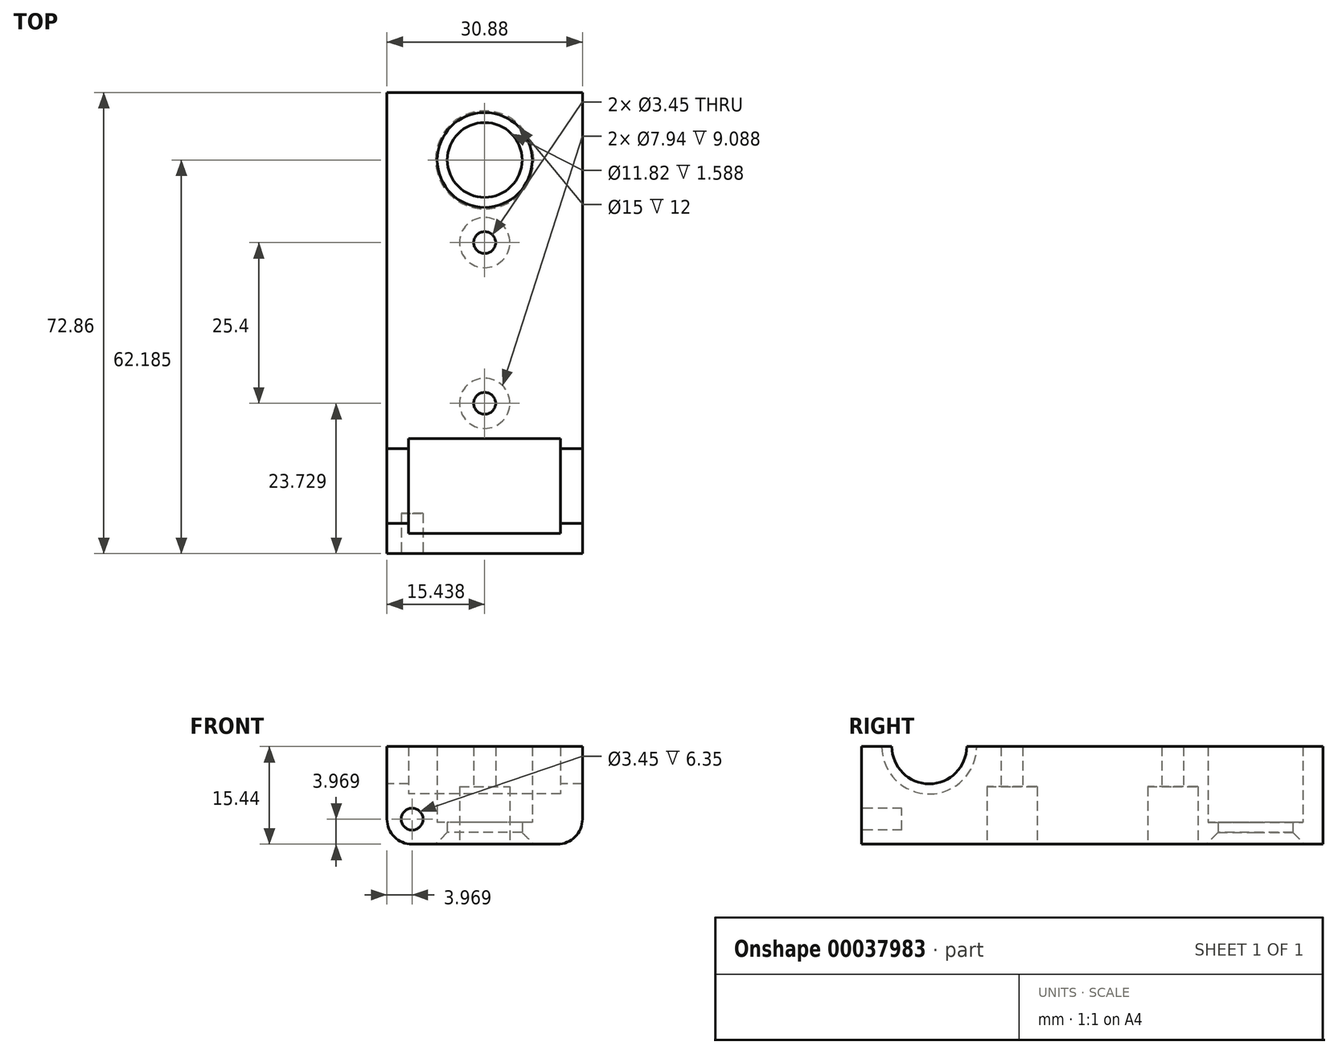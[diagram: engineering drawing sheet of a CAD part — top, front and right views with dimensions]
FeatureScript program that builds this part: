
annotation { "Feature Type Name" : "Feature", "Feature Type Description" : "" }
export const myFeature = defineFeature(function(context is Context, id is Id, definition is map)
    precondition{}
    {
        {
            var Q0;
            Q0=qCreatedBy(makeId("Top.planeOp"),FACE);
            var sketch = newSketch(context, id + "F0", { "sketchPlane" : qUnion([Q0])});
            skLineSegment(sketch, "E0.bottom", {"start": v(0, 0) * mm, "end": v(30.88, 0) * mm});
            skLineSegment(sketch, "E0.top", {"start": v(0, -72.86) * mm, "end": v(30.88, -72.86) * mm});
            skLineSegment(sketch, "E0.left", {"start": v(0, 0) * mm, "end": v(0, -72.86) * mm});
            skLineSegment(sketch, "E0.right", {"start": v(30.88, 0) * mm, "end": v(30.88, -72.86) * mm});
            skLineSegment(sketch, "E1", {"start": v(15.44, 0) * mm, "end": v(15.44, -10.67) * mm, "construction": true});
            skCircle(sketch, "E2", {"center": v(15.44, -10.67) * mm, "radius": 5.91 * mm});
            skLineSegment(sketch, "E3", {"start": v(15.44, -10.67) * mm, "end": v(15.44, -23.73) * mm, "construction": true});
            skLineSegment(sketch, "E4", {"start": v(15.44, -23.73) * mm, "end": v(15.44, -49.13) * mm, "construction": true});
            skCircle(sketch, "E5", {"center": v(15.44, -10.67) * mm, "radius": 7.5 * mm, "construction": true});
            skLineSegment(sketch, "E6", {"start": v(15.44, -49.13) * mm, "end": v(15.44, -72.86) * mm, "construction": true});
            skCircle(sketch, "E7", {"center": v(15.44, -23.73) * mm, "radius": 1.73 * mm});
            skCircle(sketch, "E8", {"center": v(15.44, -49.13) * mm, "radius": 1.73 * mm});
            skSolve(sketch);
        }
        {
            var Q0;
            Q0 = qSketchRegion(id + "F0", true);
            extrude(context, id + "F1", {"entities" : qUnion([Q0]), "depth" : 3.44 * mm});
        }
        {
            var Q0;
            Q0=makeQuery(id+"F1.opExtrude","CAP_FACE",FACE,{"disambiguationData":[OSD([sQuery(id+"F0.wireOp",EDGE,"E0.bottom"),sQuery(id+"F0.wireOp",EDGE,"E0.top"),sQuery(id+"F0.wireOp",EDGE,"E0.left"),sQuery(id+"F0.wireOp",EDGE,"E0.right"),sQuery(id+"F0.wireOp",EDGE,"E2"),sQuery(id+"F0.wireOp",EDGE,"E7"),sQuery(id+"F0.wireOp",EDGE,"E8")])],"isStart":false});
            var sketch = newSketch(context, id + "F2", { "sketchPlane" : qUnion([Q0])});
            skCircle(sketch, "E9", {"center": v(15.44, -10.67) * mm, "radius": 7.5 * mm});
            skSolve(sketch);
        }
        {
            var Q0;
            Q0=makeQuery(id+"F2.imprint","IMPRINT",FACE,{"disambiguationData":[TD([[makeQuery(id+"F2.imprint","IMPRINT",EDGE,{"derivedFrom":sQuery(id+"F2.wireOp",EDGE,"E9")}),-1.0]])]});
            extrude(context, id + "F3", {"entities" : qUnion([Q0]), "operationType" : NewBodyOperationType.ADD, "depth" : 12 * mm});
        }
        {
            var Q0;
            Q0=makeQuery(id+"F3.opExtrude","CAP_FACE",FACE,{"disambiguationData":[OSD([sQuery(id+"F0.wireOp",EDGE,"E0.bottom"),sQuery(id+"F0.wireOp",EDGE,"E0.top"),sQuery(id+"F0.wireOp",EDGE,"E0.left"),sQuery(id+"F0.wireOp",EDGE,"E0.right"),sQuery(id+"F0.wireOp",EDGE,"E7"),sQuery(id+"F0.wireOp",EDGE,"E8"),sQuery(id+"F2.wireOp",EDGE,"E9")])],"isStart":false});
            var sketch = newSketch(context, id + "F4", { "sketchPlane" : qUnion([Q0])});
            skLineSegment(sketch, "E10.bottom", {"start": v(3.44, -69.69) * mm, "end": v(27.44, -69.69) * mm});
            skLineSegment(sketch, "E10.top", {"start": v(3.44, -54.69) * mm, "end": v(27.44, -54.69) * mm});
            skLineSegment(sketch, "E10.left", {"start": v(3.44, -69.69) * mm, "end": v(3.44, -54.69) * mm});
            skLineSegment(sketch, "E10.right", {"start": v(27.44, -69.69) * mm, "end": v(27.44, -54.69) * mm});
            skLineSegment(sketch, "E11", {"start": v(15.44, -69.69) * mm, "end": v(15.44, -72.86) * mm, "construction": true});
            skSolve(sketch);
        }
        {
            var Q0;
            Q0 = qSketchRegion(id + "F4", true);
            extrude(context, id + "F5", {"entities" : qUnion([Q0]), "operationType" : NewBodyOperationType.REMOVE, "oppositeDirection" : true, "depth" : 7.5 * mm});
        }
        {
            var Q0;
            Q0=makeQuery(id+"F5.boolean.opBoolean","COPY",EDGE,{"derivedFrom":makeQuery(id+"F5.opExtrude","CAP_EDGE",EDGE,{"disambiguationData":[OSD([sQuery(id+"F4.wireOp",EDGE,"E10.top")])],"isStart":false})});
            var Q1;
            Q1=makeQuery(id+"F5.boolean.opBoolean","COPY",EDGE,{"derivedFrom":makeQuery(id+"F5.opExtrude","CAP_EDGE",EDGE,{"disambiguationData":[OSD([sQuery(id+"F4.wireOp",EDGE,"E10.bottom")])],"isStart":false})});
            fillet(context, id + "F6", {"entities" : qUnion([Q0, Q1]), "radius" : 7.5 * mm, "tangentPropagation" : true, "allowEdgeOverflow" : false});
        }
        {
            var Q0;
            {var subQ0=sQuery(id+"F0.wireOp",EDGE,"E0.left");Q0=makeQuery(id+"F3.boolean.opBoolean","MERGE",FACE,{"derivedFrom":[makeQuery(id+"F1.opExtrude","SWEPT_FACE",FACE,{"disambiguationData":[OSD([subQ0])]}),makeQuery(id+"F3.opExtrude","SWEPT_FACE",FACE,{"disambiguationData":[OSD([subQ0])]})]});}
            var sketch = newSketch(context, id + "F7", { "sketchPlane" : qUnion([Q0])});
            skArc(sketch, "E12", {"start": v(56.28, 15.44) * mm, "mid": v(62.19, 9.53) * mm, "end": v(68.1, 15.44) * mm});
            skLineSegment(sketch, "E13", {"start": v(56.28, 15.44) * mm, "end": v(68.1, 15.44) * mm});
            skSolve(sketch);
        }
        {
            var Q0;
            Q0 = qSketchRegion(id + "F7", true);
            var Q1;
            {var subQ0=sQuery(id+"F0.wireOp",EDGE,"E0.right");Q1=makeQuery(id+"F3.boolean.opBoolean","MERGE",FACE,{"derivedFrom":[makeQuery(id+"F1.opExtrude","SWEPT_FACE",FACE,{"disambiguationData":[OSD([subQ0])]}),makeQuery(id+"F3.opExtrude","SWEPT_FACE",FACE,{"disambiguationData":[OSD([subQ0])]})]});}
            extrude(context, id + "F8", {"entities" : qUnion([Q0]), "operationType" : NewBodyOperationType.REMOVE, "endBound" : BoundingType.UP_TO_SURFACE, "oppositeDirection" : true, "endBoundEntityFace" : qUnion([Q1]), "depth" : 25.4 * mm});
        }
        {
            var Q0;
            Q0=makeQuery(id+"F1.opExtrude","CAP_FACE",FACE,{"disambiguationData":[OSD([sQuery(id+"F0.wireOp",EDGE,"E0.bottom"),sQuery(id+"F0.wireOp",EDGE,"E0.top"),sQuery(id+"F0.wireOp",EDGE,"E0.left"),sQuery(id+"F0.wireOp",EDGE,"E0.right"),sQuery(id+"F0.wireOp",EDGE,"E2"),sQuery(id+"F0.wireOp",EDGE,"E7"),sQuery(id+"F0.wireOp",EDGE,"E8")])],"isStart":true});
            var sketch = newSketch(context, id + "F9", { "sketchPlane" : qUnion([Q0])});
            skCircle(sketch, "E14", {"center": v(15.44, 23.73) * mm, "radius": 3.97 * mm});
            skCircle(sketch, "E15", {"center": v(15.44, 49.13) * mm, "radius": 3.97 * mm});
            skSolve(sketch);
        }
        {
            var Q0;
            Q0 = qSketchRegion(id + "F9", true);
            extrude(context, id + "F10", {"entities" : qUnion([Q0]), "operationType" : NewBodyOperationType.REMOVE, "oppositeDirection" : true, "depth" : 9.1 * mm});
        }
        {
            var Q0;
            Q0=makeQuery(id+"F1.opExtrude","CAP_EDGE",EDGE,{"disambiguationData":[OSD([sQuery(id+"F0.wireOp",EDGE,"E0.left")])],"isStart":true});
            var Q1;
            Q1=makeQuery(id+"F1.opExtrude","CAP_EDGE",EDGE,{"disambiguationData":[OSD([sQuery(id+"F0.wireOp",EDGE,"E0.right")])],"isStart":true});
            fillet(context, id + "F11", {"entities" : qUnion([Q0, Q1]), "radius" : 3.97 * mm, "tangentPropagation" : true, "allowEdgeOverflow" : false});
        }
        {
            var Q0;
            {var subQ0=sQuery(id+"F0.wireOp",EDGE,"E0.top");Q0=makeQuery(id+"F3.boolean.opBoolean","MERGE",FACE,{"derivedFrom":[makeQuery(id+"F1.opExtrude","SWEPT_FACE",FACE,{"disambiguationData":[OSD([subQ0])]}),makeQuery(id+"F3.opExtrude","SWEPT_FACE",FACE,{"disambiguationData":[OSD([subQ0])]})]});}
            var sketch = newSketch(context, id + "F12", { "sketchPlane" : qUnion([Q0])});
            skCircle(sketch, "E16", {"center": v(3.97, 3.97) * mm, "radius": 1.73 * mm});
            skSolve(sketch);
        }
        {
            var Q0;
            Q0 = qSketchRegion(id + "F12", true);
            extrude(context, id + "F13", {"entities" : qUnion([Q0]), "operationType" : NewBodyOperationType.REMOVE, "oppositeDirection" : true, "depth" : 6.35 * mm});
        }
        {
            var Q0;
            Q0=makeQuery(id+"F1.opExtrude","CAP_EDGE",EDGE,{"disambiguationData":[OSD([sQuery(id+"F0.wireOp",EDGE,"E2")])],"isStart":true});
            var Q1;
            Q1=makeQuery(id+"F8.boolean.opBoolean","COPY",EDGE,{"derivedFrom":makeQuery(id+"F8.opExtrude","CAP_EDGE",EDGE,{"disambiguationData":[OSD([sQuery(id+"F7.wireOp",EDGE,"E12")])],"isStart":false})});
            var Q2;
            Q2=makeQuery(id+"F8.boolean.opBoolean","COPY",EDGE,{"derivedFrom":makeQuery(id+"F8.opExtrude","CAP_EDGE",EDGE,{"disambiguationData":[OSD([sQuery(id+"F7.wireOp",EDGE,"E12")])],"isStart":true})});
            chamfer(context, id + "F14", {"entities" : qUnion([Q0, Q1, Q2]), "width" : 1.85 * mm, "tangentPropagation" : true});
        }
    });
